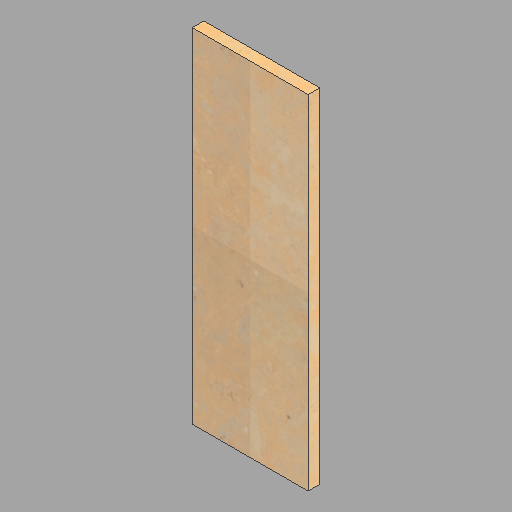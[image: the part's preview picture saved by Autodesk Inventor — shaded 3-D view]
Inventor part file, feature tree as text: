
AUTODESK INVENTOR PART (.ipt)
format: ipt  version: 2023 (Build 270158000, 158)  size: 200,704 bytes
history: native  units: in
note: dims shown in document units (in); Inventor stores cm internally (conversion verified against a paired STEP export)
features: extrude x1, sketch x1
ambient origin geometry x8: Origin, YZ Plane, XZ Plane, XY Plane, X Axis, Y Axis, Z Axis, Center Point
bodies: Solid1 (feature_tree)
feature tree (2):
  extrude  "Extrusion1"  Depth=29.625in
  sketch  "Sketch1"  dims[d0=10.0in d1=29.625in d2=1.0in d3=0.0in]
